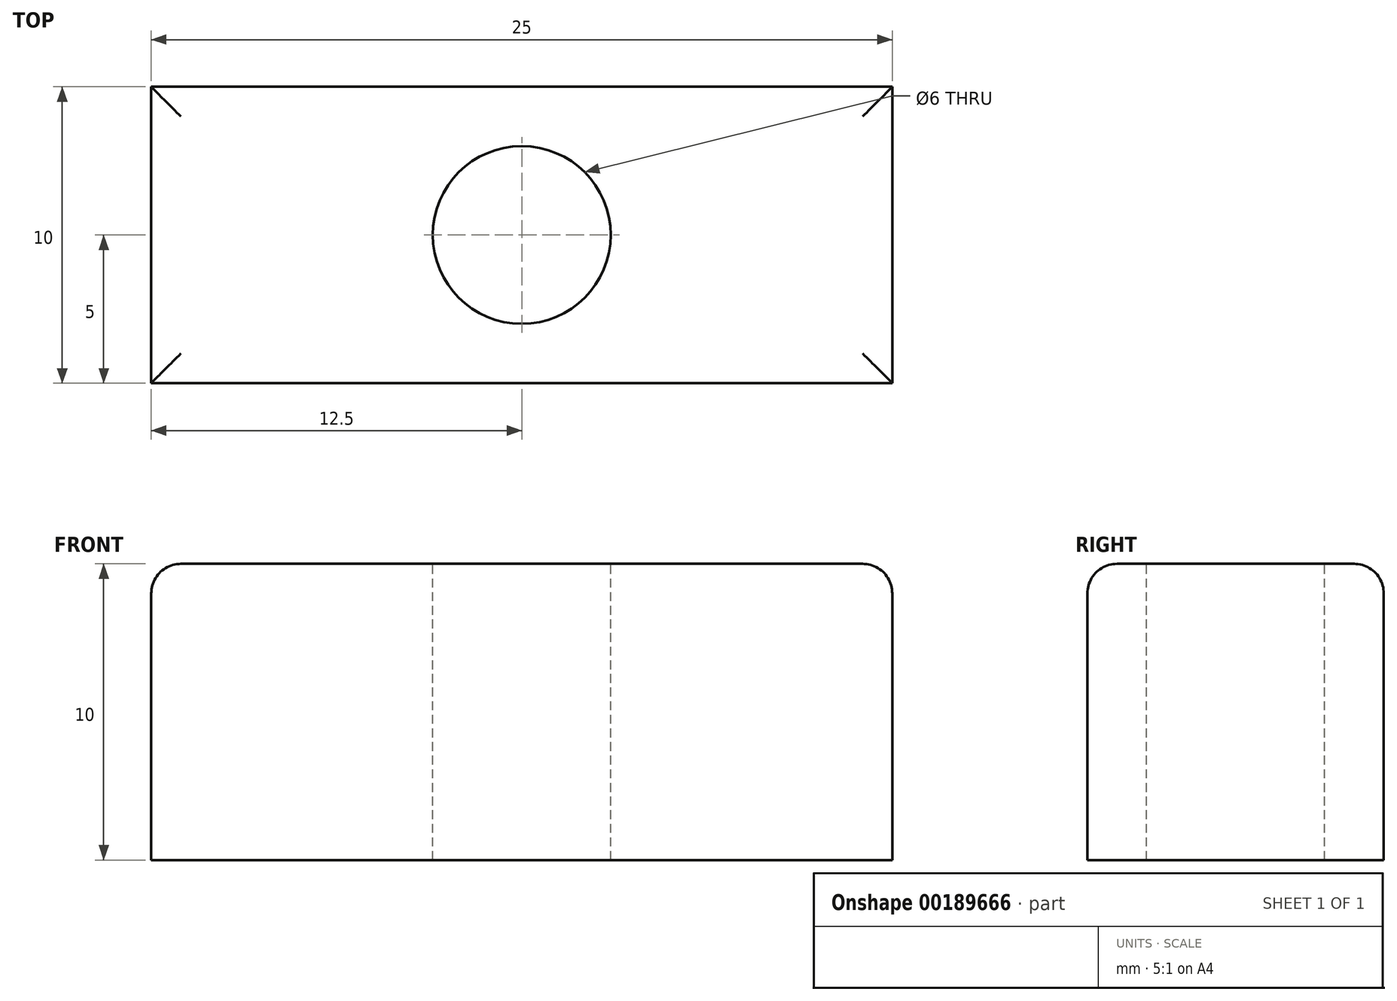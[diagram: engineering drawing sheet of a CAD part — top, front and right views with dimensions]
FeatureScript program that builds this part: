
annotation { "Feature Type Name" : "Feature", "Feature Type Description" : "" }
export const myFeature = defineFeature(function(context is Context, id is Id, definition is map)
    precondition{}
    {
        {
            var Q0;
            Q0=qCreatedBy(makeId("Top.planeOp"),FACE);
            var sketch = newSketch(context, id + "F0", { "sketchPlane" : qUnion([Q0])});
            skLineSegment(sketch, "E0.bottom", {"start": v(12.5, -5) * mm, "end": v(-12.5, -5) * mm});
            skLineSegment(sketch, "E0.top", {"start": v(12.5, 5) * mm, "end": v(-12.5, 5) * mm});
            skLineSegment(sketch, "E0.left", {"start": v(12.5, -5) * mm, "end": v(12.5, 5) * mm});
            skLineSegment(sketch, "E0.right", {"start": v(-12.5, -5) * mm, "end": v(-12.5, 5) * mm});
            skPoint(sketch, "E0.middle", {"position": v(0, 0) * mm});
            skSolve(sketch);
        }
        {
            var Q0;
            Q0=makeQuery(id+"F0.imprint","IMPRINT",FACE,{"disambiguationData":[TD([[makeQuery(id+"F0.imprint","IMPRINT",EDGE,{"derivedFrom":sQuery(id+"F0.wireOp",EDGE,"E0.bottom")}),-1.0]])]});
            extrude(context, id + "F1", {"entities" : qUnion([Q0]), "depth" : 10 * mm});
        }
        {
            var Q0;
            Q0=makeQuery(id+"F1.opExtrude","CAP_FACE",FACE,{"disambiguationData":[OSD([sQuery(id+"F0.wireOp",EDGE,"E0.bottom"),sQuery(id+"F0.wireOp",EDGE,"E0.top"),sQuery(id+"F0.wireOp",EDGE,"E0.left"),sQuery(id+"F0.wireOp",EDGE,"E0.right")])],"isStart":false});
            var sketch = newSketch(context, id + "F2", { "sketchPlane" : qUnion([Q0])});
            skCircle(sketch, "E1", {"center": v(0, 0) * mm, "radius": 1.5 * mm});
            skCircle(sketch, "E2", {"center": v(0, 0) * mm, "radius": 3 * mm});
            skSolve(sketch);
        }
        {
            var Q0;
            Q0=makeQuery(id+"F1.opExtrude","CAP_EDGE",EDGE,{"disambiguationData":[OSD([sQuery(id+"F0.wireOp",EDGE,"E0.top")])],"isStart":false});
            var Q1;
            Q1=makeQuery(id+"F1.opExtrude","CAP_EDGE",EDGE,{"disambiguationData":[OSD([sQuery(id+"F0.wireOp",EDGE,"E0.left")])],"isStart":false});
            var Q2;
            Q2=makeQuery(id+"F1.opExtrude","CAP_EDGE",EDGE,{"disambiguationData":[OSD([sQuery(id+"F0.wireOp",EDGE,"E0.bottom")])],"isStart":false});
            var Q3;
            Q3=makeQuery(id+"F1.opExtrude","CAP_EDGE",EDGE,{"disambiguationData":[OSD([sQuery(id+"F0.wireOp",EDGE,"E0.right")])],"isStart":false});
            fillet(context, id + "F3", {"entities" : qUnion([Q0, Q1, Q2, Q3]), "radius" : 1 * mm, "tangentPropagation" : true, "allowEdgeOverflow" : false});
        }
        {
            var Q0;
            Q0 = qSketchRegion(id + "F2", true);
            var Q1;
            Q1=makeQuery(id+"F2.imprint","IMPRINT",FACE,{"disambiguationData":[TD([[makeQuery(id+"F2.imprint","IMPRINT",EDGE,{"derivedFrom":sQuery(id+"F2.wireOp",EDGE,"E1")}),1.0]])]});
            extrude(context, id + "F4", {"entities" : qUnion([Q0, Q1]), "operationType" : NewBodyOperationType.REMOVE, "endBound" : BoundingType.THROUGH_ALL, "oppositeDirection" : true, "depth" : 25 * mm});
        }
    });
